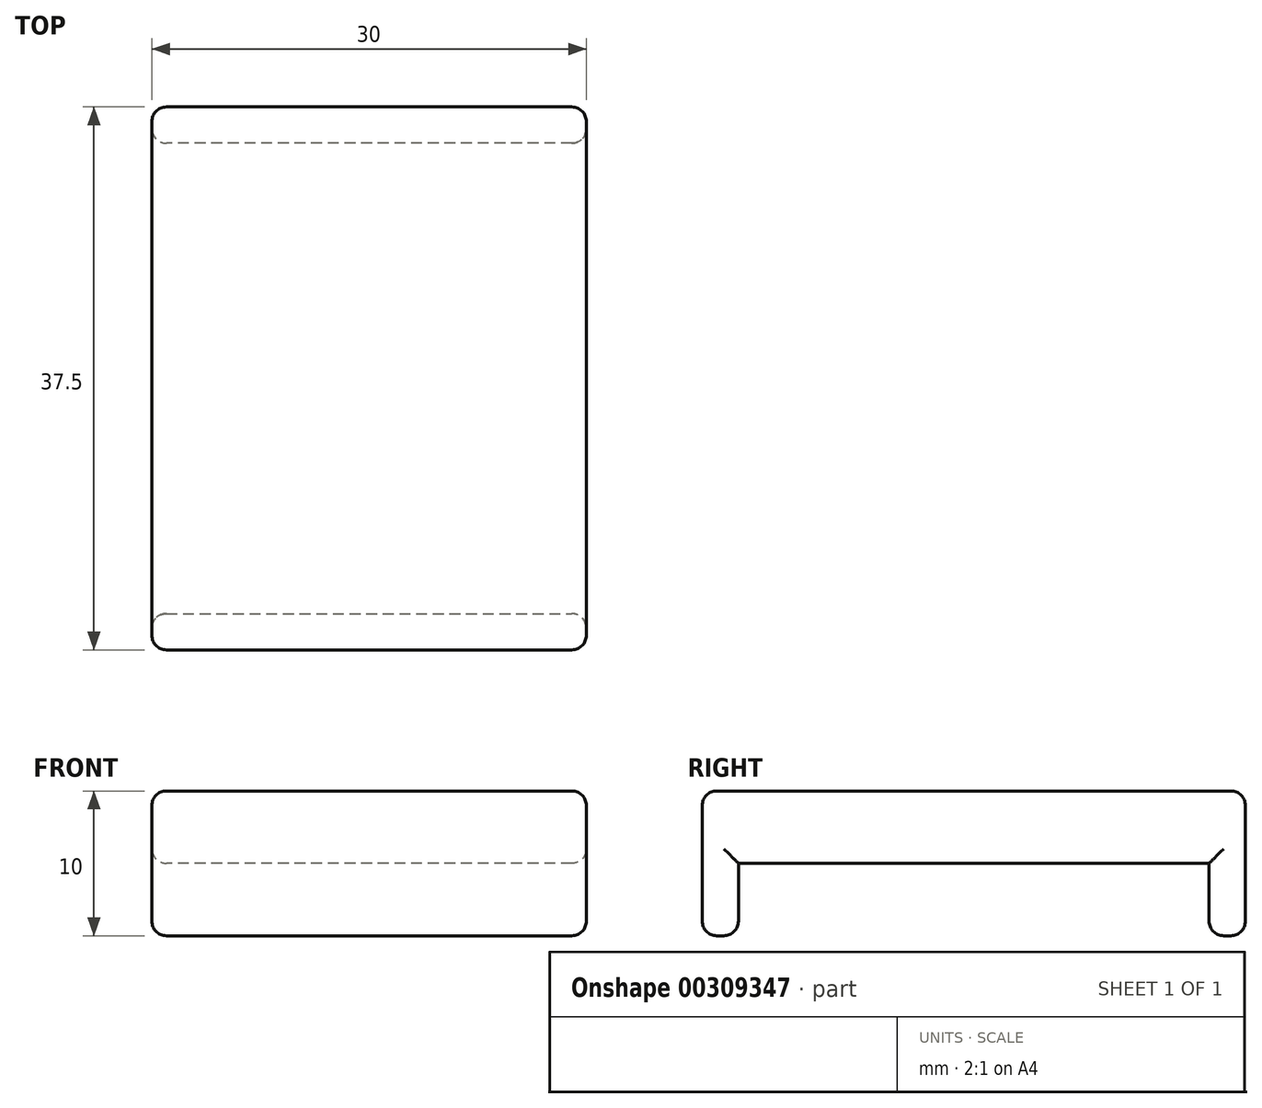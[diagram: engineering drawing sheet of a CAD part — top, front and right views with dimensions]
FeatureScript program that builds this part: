
annotation { "Feature Type Name" : "Feature", "Feature Type Description" : "" }
export const myFeature = defineFeature(function(context is Context, id is Id, definition is map)
    precondition{}
    {
        {
            var Q0;
            Q0=qCreatedBy(makeId("Top.planeOp"),FACE);
            var sketch = newSketch(context, id + "F0", { "sketchPlane" : qUnion([Q0])});
            skLineSegment(sketch, "E0.bottom", {"start": v(-12.5, 16.25) * mm, "end": v(12.5, 16.25) * mm});
            skLineSegment(sketch, "E0.top", {"start": v(-12.5, -16.25) * mm, "end": v(12.5, -16.25) * mm});
            skLineSegment(sketch, "E0.left", {"start": v(-12.5, 16.25) * mm, "end": v(-12.5, -16.25) * mm});
            skLineSegment(sketch, "E0.right", {"start": v(12.5, 16.25) * mm, "end": v(12.5, -16.25) * mm});
            skPoint(sketch, "E0.middle", {"position": v(0, 0) * mm});
            skLineSegment(sketch, "E1.bottom", {"start": v(-15, 18.75) * mm, "end": v(15, 18.75) * mm});
            skLineSegment(sketch, "E1.top", {"start": v(-15, -18.75) * mm, "end": v(15, -18.75) * mm});
            skLineSegment(sketch, "E1.left", {"start": v(-15, 18.75) * mm, "end": v(-15, -18.75) * mm});
            skLineSegment(sketch, "E1.right", {"start": v(15, 18.75) * mm, "end": v(15, -18.75) * mm});
            skLineSegment(sketch, "E2", {"start": v(-12.5, 16.25) * mm, "end": v(-15, 16.25) * mm});
            skLineSegment(sketch, "E3", {"start": v(12.5, 16.25) * mm, "end": v(15, 16.25) * mm});
            skLineSegment(sketch, "E4", {"start": v(-12.5, -16.25) * mm, "end": v(-15, -16.25) * mm});
            skLineSegment(sketch, "E5", {"start": v(12.5, -16.25) * mm, "end": v(15, -16.25) * mm});
            skSolve(sketch);
        }
        {
            var Q0;
            Q0=makeQuery(id+"F0.imprint","IMPRINT",FACE,{"disambiguationData":[TD([[makeQuery(id+"F0.imprint","IMPRINT",EDGE,{"derivedFrom":sQuery(id+"F0.wireOp",EDGE,"E0.bottom")}),-1.0]])]});
            var Q1;
            Q1=makeQuery(id+"F0.imprint","IMPRINT",FACE,{"disambiguationData":[TD([[makeQuery(id+"F0.imprint","IMPRINT",EDGE,{"derivedFrom":sQuery(id+"F0.wireOp",EDGE,"E0.bottom")}),1.0]])]});
            var Q2;
            Q2=makeQuery(id+"F0.imprint","IMPRINT",FACE,{"disambiguationData":[TD([[makeQuery(id+"F0.imprint","IMPRINT",EDGE,{"derivedFrom":sQuery(id+"F0.wireOp",EDGE,"E0.left")}),-1.0]])]});
            var Q3;
            Q3=makeQuery(id+"F0.imprint","IMPRINT",FACE,{"disambiguationData":[TD([[makeQuery(id+"F0.imprint","IMPRINT",EDGE,{"derivedFrom":sQuery(id+"F0.wireOp",EDGE,"E0.top")}),-1.0]])]});
            var Q4;
            Q4=makeQuery(id+"F0.imprint","IMPRINT",FACE,{"disambiguationData":[TD([[makeQuery(id+"F0.imprint","IMPRINT",EDGE,{"derivedFrom":sQuery(id+"F0.wireOp",EDGE,"E0.right")}),1.0]])]});
            extrude(context, id + "F1", {"entities" : qUnion([Q0, Q1, Q2, Q3, Q4]), "depth" : 5 * mm});
        }
        {
            var Q0;
            Q0=makeQuery(id+"F0.imprint","IMPRINT",FACE,{"disambiguationData":[TD([[makeQuery(id+"F0.imprint","IMPRINT",EDGE,{"derivedFrom":sQuery(id+"F0.wireOp",EDGE,"E0.top")}),-1.0]])]});
            var Q1;
            Q1=makeQuery(id+"F0.imprint","IMPRINT",FACE,{"disambiguationData":[TD([[makeQuery(id+"F0.imprint","IMPRINT",EDGE,{"derivedFrom":sQuery(id+"F0.wireOp",EDGE,"E0.bottom")}),1.0]])]});
            extrude(context, id + "F2", {"entities" : qUnion([Q0, Q1]), "operationType" : NewBodyOperationType.ADD, "oppositeDirection" : true, "depth" : 5 * mm});
        }
        {
            var Q0;
            Q0=makeQuery(id+"F2.opExtrude","CAP_FACE",FACE,{"disambiguationData":[OSD([sQuery(id+"F0.wireOp",EDGE,"E0.bottom"),sQuery(id+"F0.wireOp",EDGE,"E1.bottom"),sQuery(id+"F0.wireOp",EDGE,"E1.left"),sQuery(id+"F0.wireOp",EDGE,"E1.right"),sQuery(id+"F0.wireOp",EDGE,"E2"),sQuery(id+"F0.wireOp",EDGE,"E3")])],"isStart":false});
            var Q1;
            Q1=makeQuery(id+"F2.opExtrude","CAP_FACE",FACE,{"disambiguationData":[OSD([sQuery(id+"F0.wireOp",EDGE,"E0.top"),sQuery(id+"F0.wireOp",EDGE,"E1.top"),sQuery(id+"F0.wireOp",EDGE,"E1.left"),sQuery(id+"F0.wireOp",EDGE,"E1.right"),sQuery(id+"F0.wireOp",EDGE,"E4"),sQuery(id+"F0.wireOp",EDGE,"E5")])],"isStart":false});
            var Q2;
            Q2=makeQuery(id+"Fk8BRS8rfzKmaF9_0.opExtrude","CAP_FACE",FACE,{"disambiguationData":[OSD([sQuery(id+"F0.wireOp",EDGE,"E0.bottom"),sQuery(id+"F0.wireOp",EDGE,"E0.top"),sQuery(id+"F0.wireOp",EDGE,"E0.left"),sQuery(id+"F0.wireOp",EDGE,"E0.right"),sQuery(id+"F0.wireOp",EDGE,"E1.bottom"),sQuery(id+"F0.wireOp",EDGE,"E1.top"),sQuery(id+"F0.wireOp",EDGE,"E1.left"),sQuery(id+"F0.wireOp",EDGE,"E1.right")])],"isStart":false});
            var Q3;
            {var subQ0=sQuery(id+"F0.wireOp",EDGE,"E1.left");Q3=makeQuery(id+"F2.boolean.opBoolean","MERGE",FACE,{"derivedFrom":[makeQuery(id+"Fk8BRS8rfzKmaF9_0.boolean.opBoolean","MERGE",FACE,{"derivedFrom":[makeQuery(id+"F1.opExtrude","SWEPT_FACE",FACE,{"disambiguationData":[OSD([subQ0])]}),makeQuery(id+"Fk8BRS8rfzKmaF9_0.opExtrude","SWEPT_FACE",FACE,{"disambiguationData":[OSD([subQ0])]})]}),makeQuery(id+"F2.opExtrude","SWEPT_FACE",FACE,{"disambiguationData":[OSD([subQ0]),TDD([makeQuery(id+"F0.imprint","IMPRINT",EDGE,{"disambiguationData":[TD([[makeQuery(id+"F0.imprint","INTERSECT",VERTEX,{"derivedFrom":[sQuery(id+"F0.wireOp",EDGE,"E1.bottom"),subQ0]}),-1.0]])],"derivedFrom":subQ0})])]}),makeQuery(id+"F2.opExtrude","SWEPT_FACE",FACE,{"disambiguationData":[OSD([subQ0]),TDD([makeQuery(id+"F0.imprint","IMPRINT",EDGE,{"disambiguationData":[TD([[makeQuery(id+"F0.imprint","INTERSECT",VERTEX,{"derivedFrom":[sQuery(id+"F0.wireOp",EDGE,"E1.top"),subQ0]}),1.0]])],"derivedFrom":subQ0})])]})]});}
            var Q4;
            {var subQ0=sQuery(id+"F0.wireOp",EDGE,"E1.bottom");Q4=makeQuery(id+"F2.boolean.opBoolean","MERGE",FACE,{"derivedFrom":[makeQuery(id+"Fk8BRS8rfzKmaF9_0.boolean.opBoolean","MERGE",FACE,{"derivedFrom":[makeQuery(id+"F1.opExtrude","SWEPT_FACE",FACE,{"disambiguationData":[OSD([subQ0])]}),makeQuery(id+"Fk8BRS8rfzKmaF9_0.opExtrude","SWEPT_FACE",FACE,{"disambiguationData":[OSD([subQ0])]})]}),makeQuery(id+"F2.opExtrude","SWEPT_FACE",FACE,{"disambiguationData":[OSD([subQ0])]})]});}
            var Q5;
            {var subQ0=sQuery(id+"F0.wireOp",EDGE,"E1.right");Q5=makeQuery(id+"F2.boolean.opBoolean","MERGE",FACE,{"derivedFrom":[makeQuery(id+"Fk8BRS8rfzKmaF9_0.boolean.opBoolean","MERGE",FACE,{"derivedFrom":[makeQuery(id+"F1.opExtrude","SWEPT_FACE",FACE,{"disambiguationData":[OSD([subQ0])]}),makeQuery(id+"Fk8BRS8rfzKmaF9_0.opExtrude","SWEPT_FACE",FACE,{"disambiguationData":[OSD([subQ0])]})]}),makeQuery(id+"F2.opExtrude","SWEPT_FACE",FACE,{"disambiguationData":[OSD([subQ0]),TDD([makeQuery(id+"F0.imprint","IMPRINT",EDGE,{"disambiguationData":[TD([[makeQuery(id+"F0.imprint","INTERSECT",VERTEX,{"derivedFrom":[sQuery(id+"F0.wireOp",EDGE,"E1.bottom"),subQ0]}),-1.0]])],"derivedFrom":subQ0})])]}),makeQuery(id+"F2.opExtrude","SWEPT_FACE",FACE,{"disambiguationData":[OSD([subQ0]),TDD([makeQuery(id+"F0.imprint","IMPRINT",EDGE,{"disambiguationData":[TD([[makeQuery(id+"F0.imprint","INTERSECT",VERTEX,{"derivedFrom":[sQuery(id+"F0.wireOp",EDGE,"E1.top"),subQ0]}),1.0]])],"derivedFrom":subQ0})])]})]});}
            var Q6;
            {var subQ0=sQuery(id+"F0.wireOp",EDGE,"E1.top");Q6=makeQuery(id+"F2.boolean.opBoolean","MERGE",FACE,{"derivedFrom":[makeQuery(id+"Fk8BRS8rfzKmaF9_0.boolean.opBoolean","MERGE",FACE,{"derivedFrom":[makeQuery(id+"F1.opExtrude","SWEPT_FACE",FACE,{"disambiguationData":[OSD([subQ0])]}),makeQuery(id+"Fk8BRS8rfzKmaF9_0.opExtrude","SWEPT_FACE",FACE,{"disambiguationData":[OSD([subQ0])]})]}),makeQuery(id+"F2.opExtrude","SWEPT_FACE",FACE,{"disambiguationData":[OSD([subQ0])]})]});}
            fillet(context, id + "F3", {"entities" : qUnion([Q0, Q1, Q2, Q3, Q4, Q5, Q6]), "radius" : 1 * mm, "tangentPropagation" : true, "allowEdgeOverflow" : false});
        }
    });
